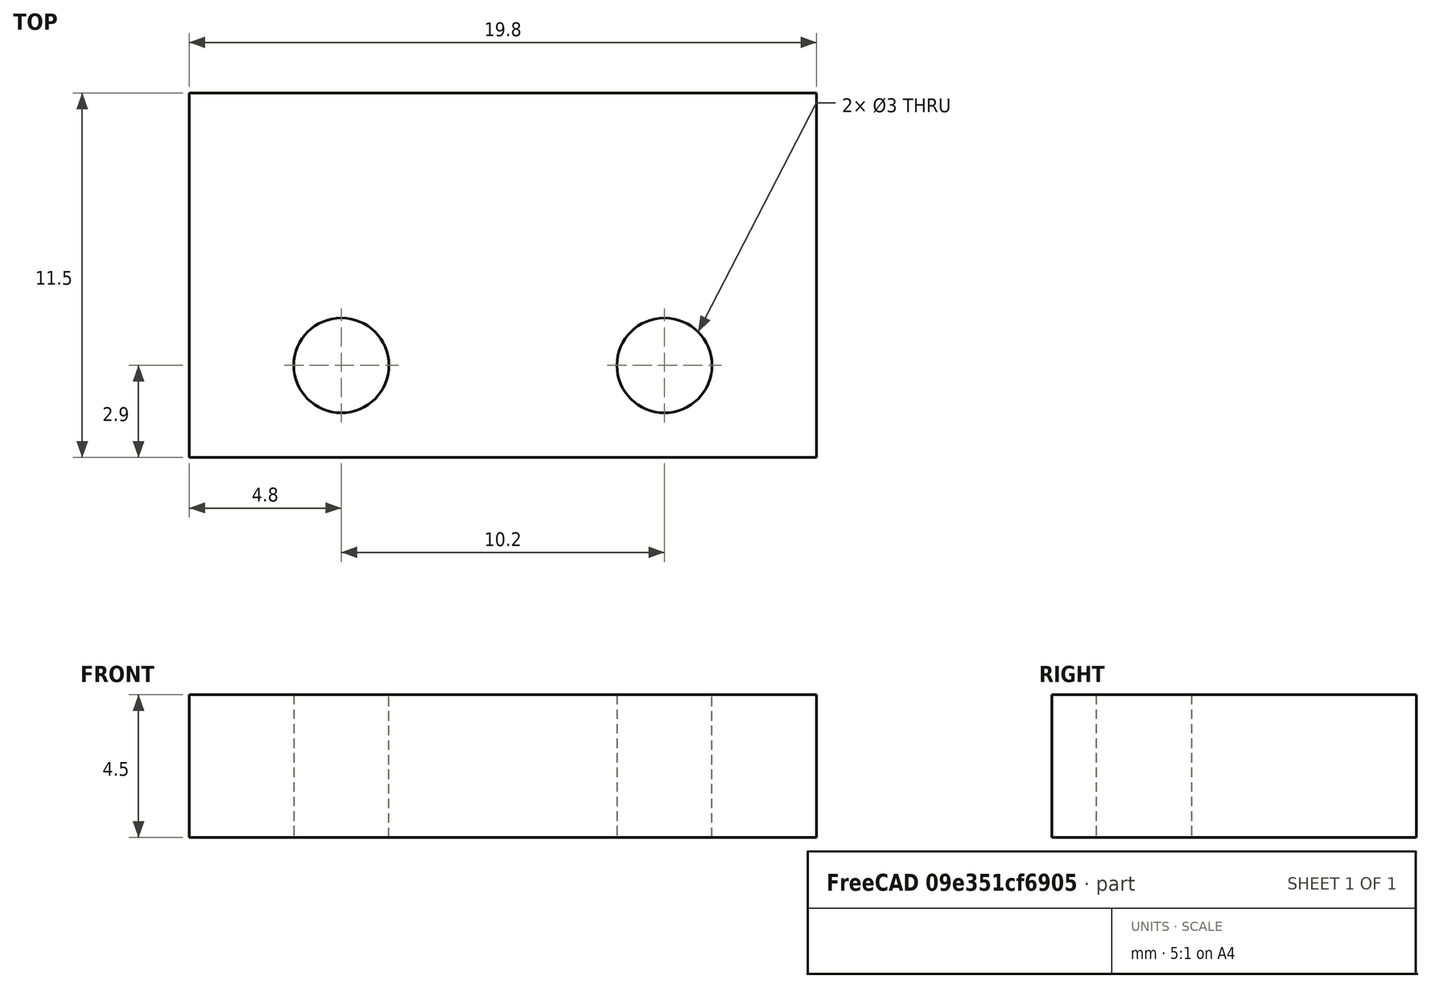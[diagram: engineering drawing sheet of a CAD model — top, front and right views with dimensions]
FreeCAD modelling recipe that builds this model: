
FCSTD DOCUMENT  (FreeCAD 0.16R6707 (Git))
Label: support_capteurs_pince
License: All rights reserved
LicenseURL: http://en.wikipedia.org/wiki/All_rights_reserved
objects: Sketcher::SketchObject×1, PartDesign::Pad×1
note: 3 computed .brp shape members not serialized (recipe doc carries the construction recipe); baked Part::Feature solids carry a one-line shape summary decoded from their .brp

FEATURE [Sketcher::SketchObject] Sketch
  sketch-geometry (6):
    g0: LineSegment StartX=0 StartY=0 StartZ=0 EndX=19.8 EndY=0 EndZ=0
    g1: LineSegment StartX=19.8 StartY=0 StartZ=0 EndX=19.8 EndY=11.5 EndZ=0
    g2: LineSegment StartX=19.8 StartY=11.5 StartZ=0 EndX=0 EndY=11.5 EndZ=0
    g3: LineSegment StartX=0 StartY=11.5 StartZ=0 EndX=0 EndY=0 EndZ=0
    g4: Circle CenterX=4.8 CenterY=2.9 CenterZ=0 NormalX=0 NormalY=0 NormalZ=1 Radius=1.5
    g5: Circle CenterX=15 CenterY=2.9 CenterZ=0 NormalX=0 NormalY=0 NormalZ=1 Radius=1.5
  constraints (17):
    c: Coincident(g0,g1)
    c: Coincident(g1,g2)
    c: Coincident(g2,g3)
    c: Coincident(g3,g0)
    c: Horizontal(g0)
    c: Horizontal(g2)
    c: Vertical(g1)
    c: Vertical(g3)
    c: Coincident(g0,g-1)
    c: Distance(g3) = 11.5
    c: Distance(g2) = 19.8
    c: DistanceY(g4,g5) = 0
    c: DistanceX(g4,g5) = 10.2
    c: DistanceX(g4) = 4.8
    c: DistanceY(g4) = 2.9
    c: Radius(g4) = 1.5
    c: Equal(g4,g5)
FEATURE [PartDesign::Pad] Pad
  Length = 4.5
  Length2 = 100
  Sketch = -> Sketch
  Type = 0
